# Revit family: Blixer 4 (a)
name_source: partatom
category: Equipement spécialisé
revit_build: Autodesk Revit LT 2015 (Build: 20140606_1530(x64)
units: mm (PartAtom-declared; Revit-internal decimal feet)

## types (5) — shared parameters
Apparent Power = 0 VA
Depth = 325 mm  [stored 1.06627 ft]
Description = BLIXER
Electrique connexion = 40 mm  [stored 0.131234 ft]
Fabricant = ROBOT COUPE
Height = 479 mm
Modèle = Blixer 4
URL = www.robot-coupe.com
Width = 291 mm
water = Connector
zero-valued in all types: Cold water supply, Cold water supply height, Top, Used water, Waste water height

## per-type parameters (varying)
| type | Amps | Cycle | HP | Phase | Speeds (Rpm) | Volts | Watts | Weight |
| Blixer 4 USA   120/60/1 |  | 60 Hz | 1.5 | 1 | 3450 | 120 V | 0 W | 34 lbs |
| Blixer 4   400/50/3 | 2 & 2.7 A | 50 Hz |  | 3 | 1500 & 3000 | 400 V | 1000 W | 17.3 kg |
| Blixer 4   220/60/3 | 3.8 & 5.2 A | 60 Hz |  | 3 | 1500 & 3000 | 220 V | 1000 W | 17.3 kg |
| Blixer 4   380/60/3 | 2 & 2.7 A | 60 Hz |  | 3 | 1500 & 3000 | 380 V | 1000 W | 17.3 kg |
| Blixer 4   220/50/3 | 2 & 2.7 A | 50 Hz |  | 3 | 1500 & 3000 | 220 V | 1000 W | 17.3 kg |

note: [stored X ft] marks values corroborated as IEEE doubles in the binary element streams (Revit-internal decimal feet)

## geometry (parser evidence)
native form markers: Blend x104, Sweep x4
no freeform markers — native parametric forms only
